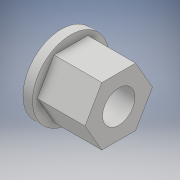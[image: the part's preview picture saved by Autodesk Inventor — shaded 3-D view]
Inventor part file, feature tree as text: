
AUTODESK INVENTOR PART (.ipt)
format: ipt  version: 2018 (Build 220112000, 112)  size: 117,760 bytes
history: native  units: mm
features: extrude x3, sketch x3
ambient origin geometry x8: Origin, YZ Plane, XZ Plane, XY Plane, X Axis, Y Axis, Z Axis, Center Point
bodies: Solid1 (feature_tree)
feature tree (6):
  extrude  "Extrusion1"  Depth=10.0mm TaperAngle=0.0deg
  extrude  "Extrusion2"  Depth=16.0mm
  extrude  "Extrusion3"  Depth=10.0mm TaperAngle=0.0deg
  sketch  "Sketch1"  dims[d0=6.1mm d1=10.0mm d2=0.0mm]
  sketch  "Sketch2"  dims[d3=6.75mm d4=16.0mm]
  sketch  "Sketch3"  dims[d5=2.0mm d6=0.0mm d7=10.0mm d8=0.0mm]
